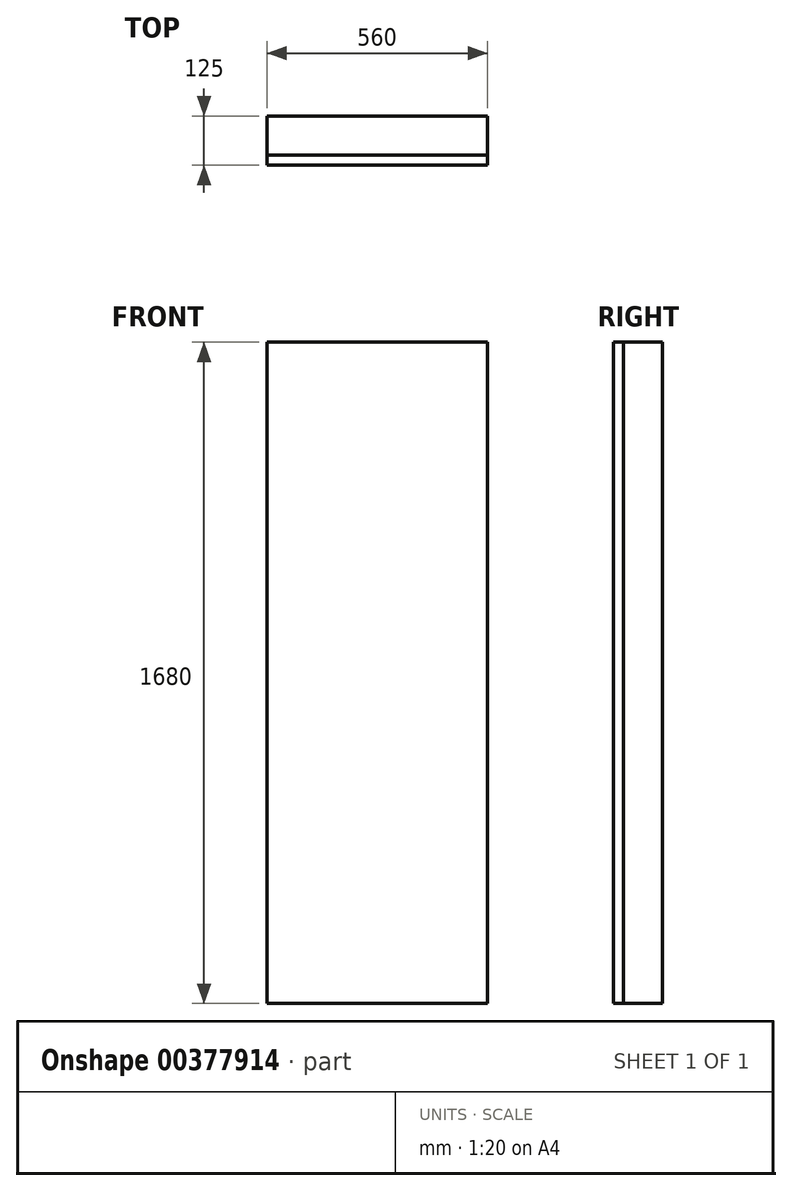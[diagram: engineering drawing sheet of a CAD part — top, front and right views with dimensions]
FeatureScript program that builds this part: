
annotation { "Feature Type Name" : "Feature", "Feature Type Description" : "" }
export const myFeature = defineFeature(function(context is Context, id is Id, definition is map)
    precondition{}
    {
        {
            var Q0;
            Q0=qCreatedBy(makeId("Front.planeOp"),FACE);
            var sketch = newSketch(context, id + "F0", { "sketchPlane" : qUnion([Q0])});
            skLineSegment(sketch, "E0.bottom", {"start": v(280, -840) * mm, "end": v(-280, -840) * mm});
            skLineSegment(sketch, "E0.top", {"start": v(280, 840) * mm, "end": v(-280, 840) * mm});
            skLineSegment(sketch, "E0.left", {"start": v(280, -840) * mm, "end": v(280, 840) * mm});
            skLineSegment(sketch, "E0.right", {"start": v(-280, -840) * mm, "end": v(-280, 840) * mm});
            skPoint(sketch, "E0.middle", {"position": v(0, 0) * mm});
            skSolve(sketch);
        }
        {
            var Q0;
            Q0 = qSketchRegion(id + "F0", true);
            extrude(context, id + "F1", {"entities" : qUnion([Q0]), "depth" : 100 * mm});
        }
        {
            var Q0;
            Q0=makeQuery(id+"F1.opExtrude","CAP_FACE",FACE,{"disambiguationData":[OSD([sQuery(id+"F0.wireOp",EDGE,"E0.bottom"),sQuery(id+"F0.wireOp",EDGE,"E0.top"),sQuery(id+"F0.wireOp",EDGE,"E0.left"),sQuery(id+"F0.wireOp",EDGE,"E0.right")])],"isStart":false});
            var sketch = newSketch(context, id + "F2", { "sketchPlane" : qUnion([Q0])});
            skLineSegment(sketch, "E1.1", {"start": v(280, -840) * mm, "end": v(-280, -840) * mm});
            skLineSegment(sketch, "E1.2", {"start": v(280, 840) * mm, "end": v(-280, 840) * mm});
            skLineSegment(sketch, "E1.3", {"start": v(280, -840) * mm, "end": v(280, 840) * mm});
            skLineSegment(sketch, "E1.4", {"start": v(-280, -840) * mm, "end": v(-280, 840) * mm});
            skPoint(sketch, "E1.5", {"position": v(0, 0) * mm});
            skSolve(sketch);
        }
        {
            var Q0;
            Q0 = qSketchRegion(id + "F2", true);
            extrude(context, id + "F3", {"entities" : qUnion([Q0]), "depth" : 25 * mm});
        }
    });
